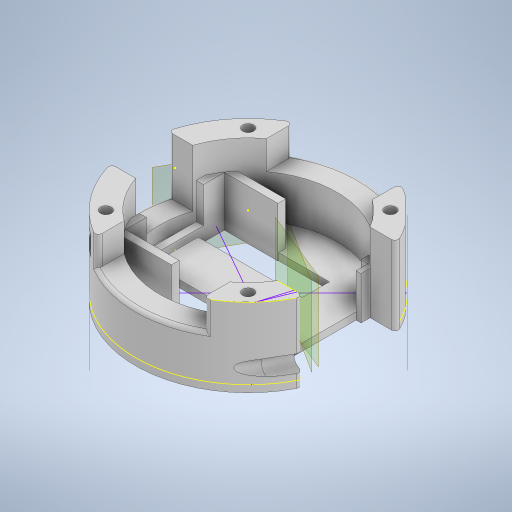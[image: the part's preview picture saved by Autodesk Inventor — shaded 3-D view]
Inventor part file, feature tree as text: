
AUTODESK INVENTOR PART (.ipt)
format: ipt  version: 2024 (Build 280153000, 153)  size: 641,536 bytes
history: native  units: in
note: dims shown in document units (in); Inventor stores cm internally (conversion verified against a paired STEP export)
features: sketch x27, extrude x20, plane x5, fillet x1
ambient origin geometry x8: Origin, YZ Plane, XZ Plane, XY Plane, X Axis, Y Axis, Z Axis, Center Point
bodies: Body1 (feature_tree)
feature tree (53):
  sketch  "Sketch2"  dims[d7=0.5512in d8=0.5512in]
  extrude  "ESP-Holder"  Depth=0.5512in
  extrude  "Outer wall"  Depth=0.5906in
  extrude  "Floor"  Depth=0.0787in
  extrude  "Vent"  Depth=0.7087in TaperAngle=0.0deg
  extrude  "SD-card"  Depth=2.4803in
  extrude  "GPIO-ACCESS"  Depth=0.0787in TaperAngle=0.0deg
  extrude  "usb"  Depth=0.6299in
  extrude  "Screw holes"  Depth=0.6299in TaperAngle=0.0deg
  extrude  "Vents"  Depth=1.9547in
  extrude  "Holders"  Depth=0.5118in
  extrude  "Extrusion16"  TaperAngle=45.0deg  [1 undecoded]
  extrude  "Extrusion17"  Depth=0.122in
  extrude  "Extrusion18"  Depth=0.0787in TaperAngle=0.0deg
  extrude  "Extrusion19"  Depth=0.1969in TaperAngle=0.0deg
  sketch  "Sketch23"  dims[d61=0.0999in d62=0.3937in d63=0.0in d64=0.315in d65=0.0in]
  sketch  "Sketch24"  dims[d66=0.7087in d67=0.0in d68=0.2362in d69=0.0in]
  extrude  "Extrusion20"  Depth=0.3937in TaperAngle=0.0deg
  fillet  "Fillet1"  Radius=0.315in
  sketch  "Sketch28"  dims[d76=0.0059in d77=0.0059in]
  sketch  "Sketch26"  dims[d74=0.0059in d75=0.0787in]
  plane  "Work Plane1"
  extrude  "Extrusion22"  Depth=0.2362in TaperAngle=0.0deg
  sketch  "Sketch29"  dims[d78=0.4724in d79=0.0787in d80=0.0in d81=0.0in d82=0.0059in d83=0.0787in d84=0.0059in d85=0.0059in]
  plane  "Work Plane2"
  extrude  "Extrusion23"  Depth=0.3937in TaperAngle=0.0deg
  sketch  "Sketch31"  dims[d88=0.0394in]
  plane  "Work Plane4"
  extrude  "Extrusion25"  Depth=0.0787in
  sketch  "Sketch35"  dims[d101=0.3937in]
  plane  "Work Plane5"
  extrude  "Extrusion26"  Depth=0.0059in
  sketch  "Sketch37"  dims[d104=0.0394in]
  plane  "Work Plane6"
  extrude  "Extrusion27"  Depth=0.0059in
  sketch  "Sketch3"  dims[d9=0.5906in d10=0.5906in]
  sketch  "Sketch5"  dims[d11=0.0787in d12=0.0787in]
  sketch  "Sketch7"  dims[d13=0.0787in d14=0.7087in d15=0.0in]
  sketch  "Sketch8"  dims[d16=1.6142in d17=2.4803in]
  sketch  "Sketch9"  dims[d18=0.7874in d19=0.0in d22=0.0787in d23=0.0in]
  sketch  "Sketch12"  dims[d32=0.315in d33=0.6299in]
  sketch  "Sketch15"  dims[d34=0.6299in d35=0.0in d36=0.6299in d37=0.0in]
  sketch  "Sketch17"  dims[d38=0.2362in d39=0.0in d42=1.9547in]
  sketch  "Sketch18"  dims[d43=0.5118in d44=0.5118in]
  sketch  "Sketch19"  dims[d45=0.7087in d46=0.0in d47=45.0deg]
  sketch  "Sketch20"  dims[d48=0.1314in d49=0.122in]
  sketch  "Sketch21"  dims[d50=1.5748in d52=360.0deg d54=0.0787in d55=0.0in]
  sketch  "Sketch22"  dims[d58=0.2968in d59=0.1969in d60=0.0in]
  sketch  "Sketch30"  dims[d86=0.3937in d87=0.0in]
  sketch  "Sketch34"  dims[d100=0.1969in]
  sketch  "Sketch36"  dims[d102=0.9843in d103=0.0in]
  sketch  "Sketch38"  dims[d105=0.0709in d106=0.1102in d107=0.0709in d108=0.1102in d109=0.3937in d110=1.1811in d111=0.6457in d112=0.0591in d113=0.0in d122=0.315in d123=0.315in d124=0.1969in d125=0.1969in d126=0.0394in d127=0.0in d128=0.189in d129=0.189in d130=0.0394in d131=0.5512in d132=0.0in d133=0.0in d135=0.189in d136=0.0394in d137=0.3937in d138=0.0in d139=0.0in]
  sketch  "Sketch25"  dims[d70=0.7087in d71=0.0in d72=0.3937in d73=0.0in]
note: 1 required parameter value undecoded (feature->parameter linkage not recoverable at this tier; creation-order binding heuristic only, values carry confidence <= 0.55)
